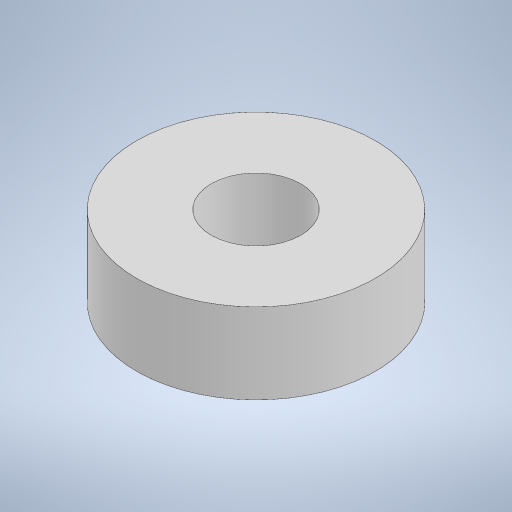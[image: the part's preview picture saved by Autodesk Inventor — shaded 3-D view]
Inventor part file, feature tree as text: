
AUTODESK INVENTOR PART (.ipt)
format: ipt  version: 2024.3 (Build 283343000, 343)  size: 204,288 bytes
history: native  units: mm
features: other x1, extrude x1, sketch x1
ambient origin geometry x8: Origin, YZ Plane, XZ Plane, XY Plane, X Axis, Y Axis, Z Axis, Center Point
bodies: Body1 (feature_tree)
feature tree (3):
  other  "Sólido1"
  extrude  "Extrusión1"  Depth=2.7mm
  sketch  "Boceto1"  dims[d0=3.0mm d1=2.5mm d2=2.7mm d3=0.0mm]
